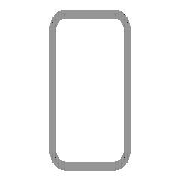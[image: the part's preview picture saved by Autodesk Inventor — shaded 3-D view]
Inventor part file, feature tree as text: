
AUTODESK INVENTOR PART (.ipt)
format: ipt  version: 2025 (Build 290162010, 162A)  size: 134,144 bytes
history: native  units: mm (DEFAULTED — no unit token found)
features: other x4, sketch x1, plane x1
ambient origin geometry x8: Origin, YZ Plane, XZ Plane, XY Plane, X Axis, Y Axis, Z Axis, Center Point
bodies: Solid1 (feature_tree), Body (feature_tree)
feature tree (6):
  parser-record x1  (decoder bookkeeping rows leaked as tree rows — omitted from the tree; the rows remain in map.json)
  other  "Driven Length"
  other  "Start Plane"
  other  "End Plane"
  sketch  "Sketch3"  dims[d3=200.0mm d4=0.0mm d7=6.0mm d9=20.0mm d11=40.0mm d12=3.0mm d13=-0.0mm d14=200.0mm d15=10.0mm d16=20.0mm d17=90.0deg d18=200.0mm]
  plane  "Work Plane3"
